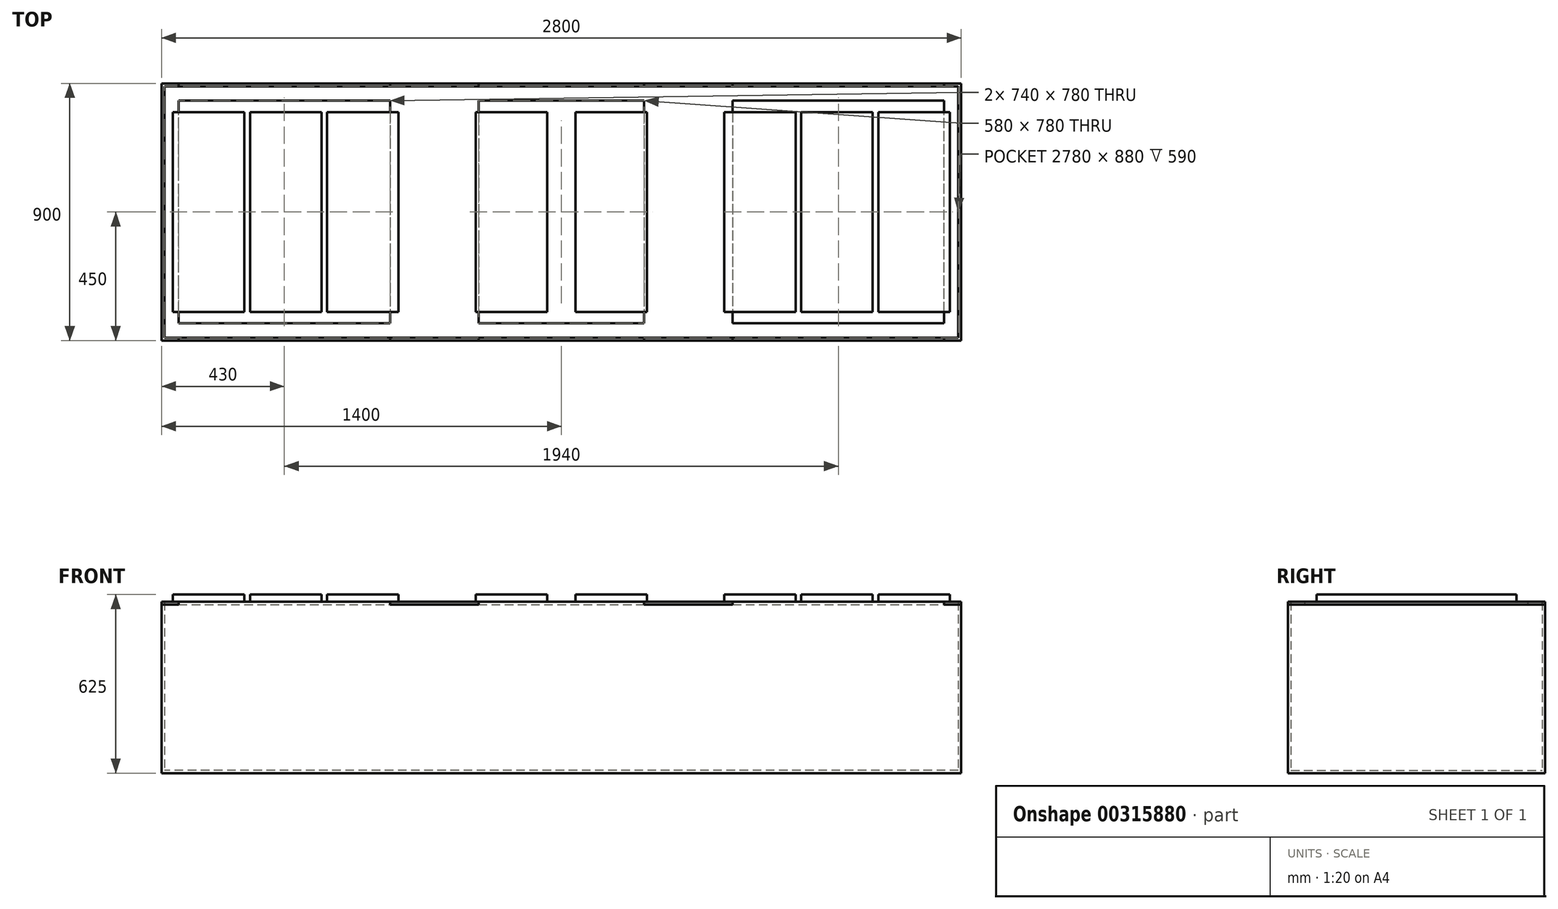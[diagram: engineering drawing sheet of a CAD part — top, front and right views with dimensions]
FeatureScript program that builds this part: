
annotation { "Feature Type Name" : "Feature", "Feature Type Description" : "" }
export const myFeature = defineFeature(function(context is Context, id is Id, definition is map)
    precondition{}
    {
        {
            var Q0;
            Q0=qCreatedBy(makeId("Top.planeOp"),FACE);
            var sketch = newSketch(context, id + "F0", { "sketchPlane" : qUnion([Q0])});
            skLineSegment(sketch, "E0.bottom", {"start": v(-1400, 450) * mm, "end": v(1400, 450) * mm});
            skLineSegment(sketch, "E0.top", {"start": v(-1400, -450) * mm, "end": v(1400, -450) * mm});
            skLineSegment(sketch, "E0.left", {"start": v(-1400, 450) * mm, "end": v(-1400, -450) * mm});
            skLineSegment(sketch, "E0.right", {"start": v(1400, 450) * mm, "end": v(1400, -450) * mm});
            skPoint(sketch, "E0.middle", {"position": v(0, 0) * mm});
            skLineSegment(sketch, "E1.bottom", {"start": v(-1390, 440) * mm, "end": v(1390, 440) * mm});
            skLineSegment(sketch, "E1.top", {"start": v(-1390, -440) * mm, "end": v(1390, -440) * mm});
            skLineSegment(sketch, "E1.left", {"start": v(-1390, 440) * mm, "end": v(-1390, -440) * mm});
            skLineSegment(sketch, "E1.right", {"start": v(1390, 440) * mm, "end": v(1390, -440) * mm});
            skSolve(sketch);
        }
        {
            var Q0;
            Q0 = qSketchRegion(id + "F0", true);
            extrude(context, id + "F1", {"entities" : qUnion([Q0]), "depth" : 600 * mm});
        }
        {
            var Q0;
            Q0=makeQuery(id+"F1.opExtrude","CAP_FACE",FACE,{"disambiguationData":[OSD([sQuery(id+"F0.wireOp",EDGE,"E0.bottom"),sQuery(id+"F0.wireOp",EDGE,"E0.top"),sQuery(id+"F0.wireOp",EDGE,"E0.left"),sQuery(id+"F0.wireOp",EDGE,"E0.right"),sQuery(id+"F0.wireOp",EDGE,"E1.bottom"),sQuery(id+"F0.wireOp",EDGE,"E1.top"),sQuery(id+"F0.wireOp",EDGE,"E1.left"),sQuery(id+"F0.wireOp",EDGE,"E1.right")])],"isStart":true});
            var sketch = newSketch(context, id + "F2", { "sketchPlane" : qUnion([Q0])});
            skLineSegment(sketch, "E2.bottom", {"start": v(-1400, -450) * mm, "end": v(1400, -450) * mm});
            skLineSegment(sketch, "E2.top", {"start": v(-1400, 450) * mm, "end": v(1400, 450) * mm});
            skLineSegment(sketch, "E2.left", {"start": v(-1400, -450) * mm, "end": v(-1400, 450) * mm});
            skLineSegment(sketch, "E2.right", {"start": v(1400, -450) * mm, "end": v(1400, 450) * mm});
            skPoint(sketch, "E2.middle", {"position": v(0, 0) * mm});
            skSolve(sketch);
        }
        {
            var Q0;
            Q0 = qSketchRegion(id + "F2", true);
            extrude(context, id + "F3", {"entities" : qUnion([Q0]), "operationType" : NewBodyOperationType.ADD, "oppositeDirection" : true, "depth" : 10 * mm});
        }
        {
            var Q0;
            Q0=makeQuery(id+"F1.opExtrude","CAP_FACE",FACE,{"disambiguationData":[OSD([sQuery(id+"F0.wireOp",EDGE,"E0.bottom"),sQuery(id+"F0.wireOp",EDGE,"E0.top"),sQuery(id+"F0.wireOp",EDGE,"E0.left"),sQuery(id+"F0.wireOp",EDGE,"E0.right"),sQuery(id+"F0.wireOp",EDGE,"E1.bottom"),sQuery(id+"F0.wireOp",EDGE,"E1.top"),sQuery(id+"F0.wireOp",EDGE,"E1.left"),sQuery(id+"F0.wireOp",EDGE,"E1.right")])],"isStart":false});
            var sketch = newSketch(context, id + "F4", { "sketchPlane" : qUnion([Q0])});
            skLineSegment(sketch, "E3.bottom", {"start": v(-1400, -450) * mm, "end": v(-1340, -450) * mm});
            skLineSegment(sketch, "E3.top", {"start": v(-1400, 450) * mm, "end": v(-1340, 450) * mm});
            skLineSegment(sketch, "E3.left", {"start": v(-1400, -450) * mm, "end": v(-1400, 450) * mm});
            skLineSegment(sketch, "E3.right", {"start": v(-1340, -450) * mm, "end": v(-1340, -440) * mm});
            skLineSegment(sketch, "E4.bottom", {"start": v(-600, 450) * mm, "end": v(-290, 450) * mm});
            skLineSegment(sketch, "E4.top", {"start": v(-600, -450) * mm, "end": v(-290, -450) * mm});
            skLineSegment(sketch, "E4.left", {"start": v(-600, 450) * mm, "end": v(-600, 440) * mm});
            skLineSegment(sketch, "E4.right", {"start": v(-290, 450) * mm, "end": v(-290, 440) * mm});
            skLineSegment(sketch, "E5", {"start": v(0, 0) * mm, "end": v(0, 217.45) * mm, "construction": true});
            skLineSegment(sketch, "E6.MirrorCS", {"start": v(600, 450) * mm, "end": v(600, 440) * mm});
            skLineSegment(sketch, "E7.MirrorCS", {"start": v(600, -450) * mm, "end": v(290, -450) * mm});
            skLineSegment(sketch, "E8.MirrorCS", {"start": v(600, 450) * mm, "end": v(290, 450) * mm});
            skLineSegment(sketch, "E9.MirrorCS", {"start": v(290, 450) * mm, "end": v(290, 440) * mm});
            skLineSegment(sketch, "E10.MirrorCS", {"start": v(1400, -450) * mm, "end": v(1340, -450) * mm});
            skLineSegment(sketch, "E11.MirrorCS", {"start": v(1400, 450) * mm, "end": v(1340, 450) * mm});
            skLineSegment(sketch, "E12.MirrorCS", {"start": v(1400, -450) * mm, "end": v(1400, 450) * mm});
            skLineSegment(sketch, "E13.MirrorCS", {"start": v(1340, -450) * mm, "end": v(1340, -440) * mm});
            skLineSegment(sketch, "E14.bottom", {"start": v(-1390, 440) * mm, "end": v(1400, 440) * mm});
            skLineSegment(sketch, "E14.top", {"start": v(-1340, 390) * mm, "end": v(-600, 390) * mm});
            skLineSegment(sketch, "E14.left", {"start": v(-1390, 440) * mm, "end": v(-1390, 390) * mm});
            skLineSegment(sketch, "E14.right", {"start": v(1400, 440) * mm, "end": v(1400, 390) * mm});
            skLineSegment(sketch, "E15", {"start": v(0, 0) * mm, "end": v(194.9, 0) * mm, "construction": true});
            skLineSegment(sketch, "E16.MirrorCS", {"start": v(1400, -440) * mm, "end": v(1400, -390) * mm});
            skLineSegment(sketch, "E17.MirrorCS", {"start": v(-1390, -440) * mm, "end": v(-1390, -390) * mm});
            skLineSegment(sketch, "E18.MirrorCS", {"start": v(-1340, -390) * mm, "end": v(-600, -390) * mm});
            skLineSegment(sketch, "E19.MirrorCS", {"start": v(-1390, -440) * mm, "end": v(1400, -440) * mm});
            skLineSegment(sketch, "E20.trimOffspring", {"start": v(-290, 390) * mm, "end": v(290, 390) * mm});
            skLineSegment(sketch, "E21.trimOffspring", {"start": v(-290, -390) * mm, "end": v(290, -390) * mm});
            skLineSegment(sketch, "E22.trimOffspring", {"start": v(600, -390) * mm, "end": v(1340, -390) * mm});
            skLineSegment(sketch, "E23.trimOffspring", {"start": v(600, 390) * mm, "end": v(1340, 390) * mm});
            skLineSegment(sketch, "E24.trimOffspring", {"start": v(-1340, 440) * mm, "end": v(-1340, 450) * mm});
            skLineSegment(sketch, "E25.trimOffspring", {"start": v(-1340, -390) * mm, "end": v(-1340, 390) * mm});
            skLineSegment(sketch, "E26.trimOffspring", {"start": v(-600, 390) * mm, "end": v(-600, -390) * mm});
            skLineSegment(sketch, "E27.trimOffspring", {"start": v(-600, -440) * mm, "end": v(-600, -450) * mm});
            skLineSegment(sketch, "E28.trimOffspring", {"start": v(-290, -440) * mm, "end": v(-290, -450) * mm});
            skLineSegment(sketch, "E29.trimOffspring", {"start": v(-290, 390) * mm, "end": v(-290, -390) * mm});
            skLineSegment(sketch, "E30.trimOffspring", {"start": v(290, 390) * mm, "end": v(290, -390) * mm});
            skLineSegment(sketch, "E31.trimOffspring", {"start": v(600, 390) * mm, "end": v(600, -390) * mm});
            skLineSegment(sketch, "E32.trimOffspring", {"start": v(290, -440) * mm, "end": v(290, -450) * mm});
            skLineSegment(sketch, "E33.trimOffspring", {"start": v(600, -440) * mm, "end": v(600, -450) * mm});
            skLineSegment(sketch, "E34.trimOffspring", {"start": v(1340, 440) * mm, "end": v(1340, 450) * mm});
            skLineSegment(sketch, "E35.trimOffspring", {"start": v(1340, -390) * mm, "end": v(1340, 390) * mm});
            skSolve(sketch);
        }
        {
            var Q0;
            Q0 = qSketchRegion(id + "F4", true);
            extrude(context, id + "F5", {"entities" : qUnion([Q0]), "oppositeDirection" : true, "depth" : 10 * mm});
        }
        {
            var Q0;
            Q0=makeQuery(id+"F5.opExtrude","CAP_FACE",FACE,{"disambiguationData":[OSD([sQuery(id+"F4.wireOp",EDGE,"E3.top"),sQuery(id+"F4.wireOp",EDGE,"E3.left"),sQuery(id+"F4.wireOp",EDGE,"E3.right"),sQuery(id+"F4.wireOp",EDGE,"E4.bottom"),sQuery(id+"F4.wireOp",EDGE,"E4.left"),sQuery(id+"F4.wireOp",EDGE,"E4.right"),sQuery(id+"F4.wireOp",EDGE,"E6.MirrorCS"),sQuery(id+"F4.wireOp",EDGE,"E8.MirrorCS"),sQuery(id+"F4.wireOp",EDGE,"E9.MirrorCS"),sQuery(id+"F4.wireOp",EDGE,"E11.MirrorCS"),sQuery(id+"F4.wireOp",EDGE,"E12.MirrorCS"),sQuery(id+"F4.wireOp",EDGE,"E13.MirrorCS"),sQuery(id+"F4.wireOp",EDGE,"E14.bottom"),sQuery(id+"F4.wireOp",EDGE,"E14.top"),sQuery(id+"F4.wireOp",EDGE,"E14.right"),sQuery(id+"F4.wireOp",EDGE,"E10.MirrorCS"),sQuery(id+"F4.wireOp",EDGE,"E16.MirrorCS"),sQuery(id+"F4.wireOp",EDGE,"E3.bottom"),sQuery(id+"F4.wireOp",EDGE,"E7.MirrorCS"),sQuery(id+"F4.wireOp",EDGE,"E18.MirrorCS"),sQuery(id+"F4.wireOp",EDGE,"E19.MirrorCS"),sQuery(id+"F4.wireOp",EDGE,"E4.top"),sQuery(id+"F4.wireOp",EDGE,"E20.trimOffspring"),sQuery(id+"F4.wireOp",EDGE,"E21.trimOffspring"),sQuery(id+"F4.wireOp",EDGE,"E22.trimOffspring"),sQuery(id+"F4.wireOp",EDGE,"E23.trimOffspring"),sQuery(id+"F4.wireOp",EDGE,"E24.trimOffspring"),sQuery(id+"F4.wireOp",EDGE,"E25.trimOffspring"),sQuery(id+"F4.wireOp",EDGE,"E26.trimOffspring"),sQuery(id+"F4.wireOp",EDGE,"E27.trimOffspring"),sQuery(id+"F4.wireOp",EDGE,"E28.trimOffspring"),sQuery(id+"F4.wireOp",EDGE,"E29.trimOffspring"),sQuery(id+"F4.wireOp",EDGE,"E30.trimOffspring"),sQuery(id+"F4.wireOp",EDGE,"E31.trimOffspring"),sQuery(id+"F4.wireOp",EDGE,"E32.trimOffspring"),sQuery(id+"F4.wireOp",EDGE,"E33.trimOffspring"),sQuery(id+"F4.wireOp",EDGE,"E34.trimOffspring"),sQuery(id+"F4.wireOp",EDGE,"E35.trimOffspring")])],"isStart":true});
            var sketch = newSketch(context, id + "F6", { "sketchPlane" : qUnion([Q0])});
            skLineSegment(sketch, "E36", {"start": v(0, 0) * mm, "end": v(0, 730.29) * mm, "construction": true});
            skPoint(sketch, "E36.endSnap0", {"position": v(0, 390) * mm});
            skLineSegment(sketch, "E37.bottom", {"start": v(-1360, 350) * mm, "end": v(-1110, 350) * mm});
            skLineSegment(sketch, "E37.top", {"start": v(-1360, -350) * mm, "end": v(-1110, -350) * mm});
            skLineSegment(sketch, "E37.left", {"start": v(-1360, 350) * mm, "end": v(-1360, -350) * mm});
            skLineSegment(sketch, "E37.right", {"start": v(-1110, 350) * mm, "end": v(-1110, -350) * mm});
            skLineSegment(sketch, "E38.bottom", {"start": v(-1090, 350) * mm, "end": v(-840, 350) * mm});
            skLineSegment(sketch, "E38.top", {"start": v(-1090, -350) * mm, "end": v(-840, -350) * mm});
            skLineSegment(sketch, "E38.left", {"start": v(-1090, 350) * mm, "end": v(-1090, -350) * mm});
            skLineSegment(sketch, "E38.right", {"start": v(-840, 350) * mm, "end": v(-840, -350) * mm});
            skLineSegment(sketch, "E39.bottom", {"start": v(-820, 350) * mm, "end": v(-570, 350) * mm});
            skLineSegment(sketch, "E39.top", {"start": v(-820, -350) * mm, "end": v(-570, -350) * mm});
            skLineSegment(sketch, "E39.left", {"start": v(-820, 350) * mm, "end": v(-820, -350) * mm});
            skLineSegment(sketch, "E39.right", {"start": v(-570, 350) * mm, "end": v(-570, -350) * mm});
            skLineSegment(sketch, "E40.bottom", {"start": v(-300, 350) * mm, "end": v(-50, 350) * mm});
            skLineSegment(sketch, "E40.top", {"start": v(-300, -350) * mm, "end": v(-50, -350) * mm});
            skLineSegment(sketch, "E40.left", {"start": v(-300, 350) * mm, "end": v(-300, -350) * mm});
            skLineSegment(sketch, "E40.right", {"start": v(-50, 350) * mm, "end": v(-50, -350) * mm});
            skLineSegment(sketch, "E41.MirrorCS", {"start": v(300, 350) * mm, "end": v(300, -350) * mm});
            skLineSegment(sketch, "E42.MirrorCS", {"start": v(840, 350) * mm, "end": v(840, -350) * mm});
            skLineSegment(sketch, "E43.MirrorCS", {"start": v(1090, 350) * mm, "end": v(1090, -350) * mm});
            skLineSegment(sketch, "E44.MirrorCS", {"start": v(1090, -350) * mm, "end": v(840, -350) * mm});
            skLineSegment(sketch, "E45.MirrorCS", {"start": v(1090, 350) * mm, "end": v(840, 350) * mm});
            skLineSegment(sketch, "E46.MirrorCS", {"start": v(570, 350) * mm, "end": v(570, -350) * mm});
            skLineSegment(sketch, "E47.MirrorCS", {"start": v(50, 350) * mm, "end": v(50, -350) * mm});
            skLineSegment(sketch, "E48.MirrorCS", {"start": v(1110, 350) * mm, "end": v(1110, -350) * mm});
            skLineSegment(sketch, "E49.MirrorCS", {"start": v(1360, 350) * mm, "end": v(1360, -350) * mm});
            skLineSegment(sketch, "E50.MirrorCS", {"start": v(1360, -350) * mm, "end": v(1110, -350) * mm});
            skLineSegment(sketch, "E51.MirrorCS", {"start": v(1360, 350) * mm, "end": v(1110, 350) * mm});
            skLineSegment(sketch, "E52.MirrorCS", {"start": v(820, 350) * mm, "end": v(820, -350) * mm});
            skLineSegment(sketch, "E53.MirrorCS", {"start": v(820, -350) * mm, "end": v(570, -350) * mm});
            skLineSegment(sketch, "E54.MirrorCS", {"start": v(820, 350) * mm, "end": v(570, 350) * mm});
            skLineSegment(sketch, "E55.MirrorCS", {"start": v(300, 350) * mm, "end": v(50, 350) * mm});
            skLineSegment(sketch, "E56.MirrorCS", {"start": v(300, -350) * mm, "end": v(50, -350) * mm});
            skSolve(sketch);
        }
        {
            var Q0;
            Q0 = qSketchRegion(id + "F6", true);
            extrude(context, id + "F7", {"entities" : qUnion([Q0]), "depth" : 25 * mm});
        }
    });
